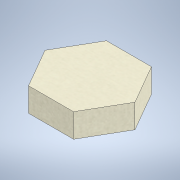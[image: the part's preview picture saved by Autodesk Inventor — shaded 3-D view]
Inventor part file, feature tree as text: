
AUTODESK INVENTOR PART (.ipt)
format: ipt  version: 2021 (Build 250183000, 183)  size: 104,960 bytes
history: native  units: mm
features: extrude x1, sketch x1
ambient origin geometry x8: Origin, YZ Plane, XZ Plane, XY Plane, X Axis, Y Axis, Z Axis, Center Point
bodies: Solid1 (feature_tree)
feature tree (2):
  extrude  "Extrusion1"  Depth=30.9mm TaperAngle=0.0deg
  sketch  "Sketch1"  dims[d0=101.0mm d1=30.9mm d2=0.0mm]
